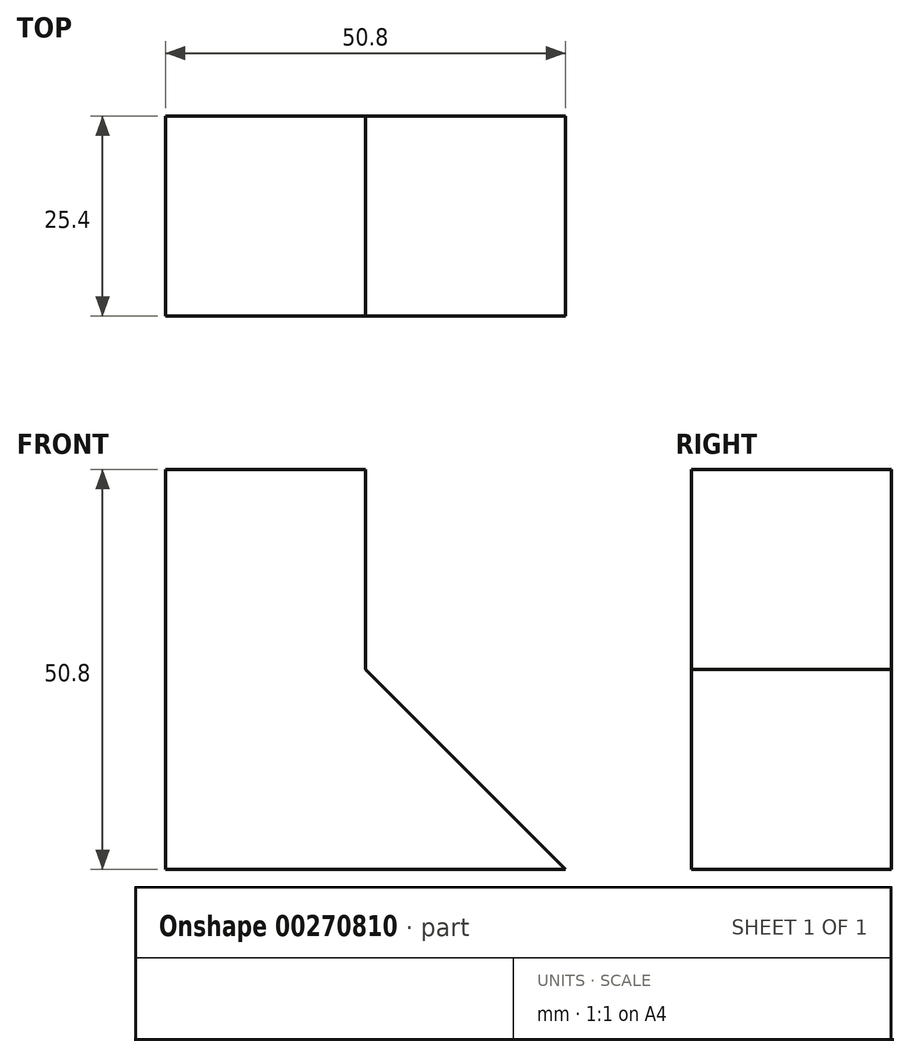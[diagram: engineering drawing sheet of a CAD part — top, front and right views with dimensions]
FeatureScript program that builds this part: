
annotation { "Feature Type Name" : "Feature", "Feature Type Description" : "" }
export const myFeature = defineFeature(function(context is Context, id is Id, definition is map)
    precondition{}
    {
        {
            var Q0;
            Q0=qCreatedBy(makeId("Front.planeOp"),FACE);
            var sketch = newSketch(context, id + "F0", { "sketchPlane" : qUnion([Q0])});
            skLineSegment(sketch, "E0", {"start": v(0, 0) * mm, "end": v(-50.8, 0) * mm});
            skLineSegment(sketch, "E1", {"start": v(-50.8, 0) * mm, "end": v(-50.8, 50.8) * mm});
            skLineSegment(sketch, "E2", {"start": v(-50.8, 50.8) * mm, "end": v(-25.4, 50.8) * mm});
            skLineSegment(sketch, "E3", {"start": v(-25.4, 50.8) * mm, "end": v(-25.4, 25.4) * mm});
            skLineSegment(sketch, "E4", {"start": v(-25.4, 25.4) * mm, "end": v(0, 0) * mm});
            skSolve(sketch);
        }
        {
            var Q0;
            Q0=makeQuery(id+"F0.imprint","IMPRINT",FACE,{"disambiguationData":[TD([[makeQuery(id+"F0.imprint","IMPRINT",EDGE,{"derivedFrom":sQuery(id+"F0.wireOp",EDGE,"E0")}),-1.0]])]});
            extrude(context, id + "F1", {"entities" : qUnion([Q0]), "depth" : 25.4 * mm});
        }
    });
